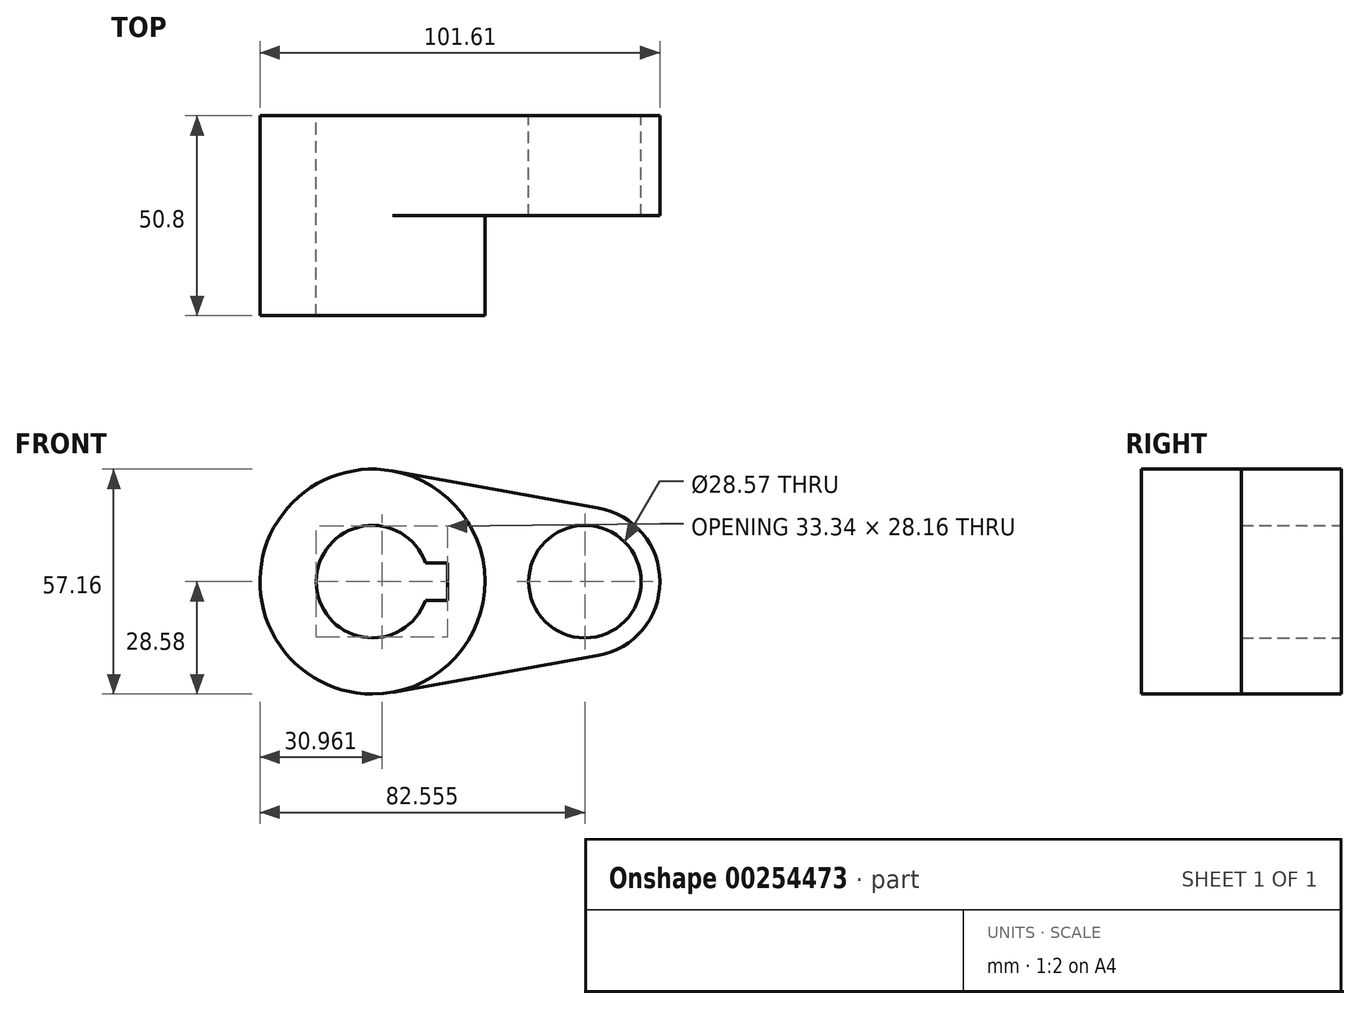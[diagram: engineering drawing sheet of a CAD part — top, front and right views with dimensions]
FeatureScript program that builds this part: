
annotation { "Feature Type Name" : "Feature", "Feature Type Description" : "" }
export const myFeature = defineFeature(function(context is Context, id is Id, definition is map)
    precondition{}
    {
        {
            var Q0;
            Q0=qCreatedBy(makeId("Front.planeOp"),FACE);
            var sketch = newSketch(context, id + "F0", { "sketchPlane" : qUnion([Q0])});
            skCircle(sketch, "E0", {"center": v(0, 0) * mm, "radius": 28.58 * mm});
            skCircle(sketch, "E1", {"center": v(53.98, 0) * mm, "radius": 19.05 * mm});
            skCircle(sketch, "E2", {"center": v(0, 0) * mm, "radius": 14.29 * mm});
            skCircle(sketch, "E3", {"center": v(53.98, 0) * mm, "radius": 14.29 * mm});
            skLineSegment(sketch, "E4.bottom", {"start": v(-19.05, -4.76) * mm, "end": v(19.05, -4.76) * mm});
            skLineSegment(sketch, "E4.top", {"start": v(-19.05, 4.76) * mm, "end": v(19.05, 4.76) * mm});
            skLineSegment(sketch, "E4.left", {"start": v(-19.05, -4.76) * mm, "end": v(-19.05, 4.76) * mm});
            skLineSegment(sketch, "E4.right", {"start": v(19.05, -4.76) * mm, "end": v(19.05, 4.76) * mm});
            skLineSegment(sketch, "E5", {"start": v(5.04, 28.13) * mm, "end": v(57.34, 18.75) * mm});
            skLineSegment(sketch, "E6", {"start": v(5.04, -28.13) * mm, "end": v(57.34, -18.75) * mm});
            skSolve(sketch);
        }
        {
            var Q0;
            Q0 = qSketchRegion(id + "F0", true);
            extrude(context, id + "F1", {"entities" : qUnion([Q0]), "depth" : 25.4 * mm});
        }
        {
            var Q0;
            {var subQ10=sQuery(id+"F0.wireOp",EDGE,"E4.left");Q0=makeQuery(id+"F0.imprint","IMPRINT",FACE,{"disambiguationData":[TD([[makeQuery(id+"F0.imprint","IMPRINT",EDGE,{"derivedFrom":subQ10}),1.0]])]});}
            var Q1;
            {var subQ5=sQuery(id+"F0.wireOp",EDGE,"E4.left");Q1=makeQuery(id+"F0.imprint","IMPRINT",FACE,{"disambiguationData":[TD([[makeQuery(id+"F0.imprint","IMPRINT",EDGE,{"derivedFrom":subQ5}),-1.0]])]});}
            extrude(context, id + "F2", {"entities" : qUnion([Q0, Q1]), "operationType" : NewBodyOperationType.ADD, "depth" : 50.8 * mm});
        }
    });
